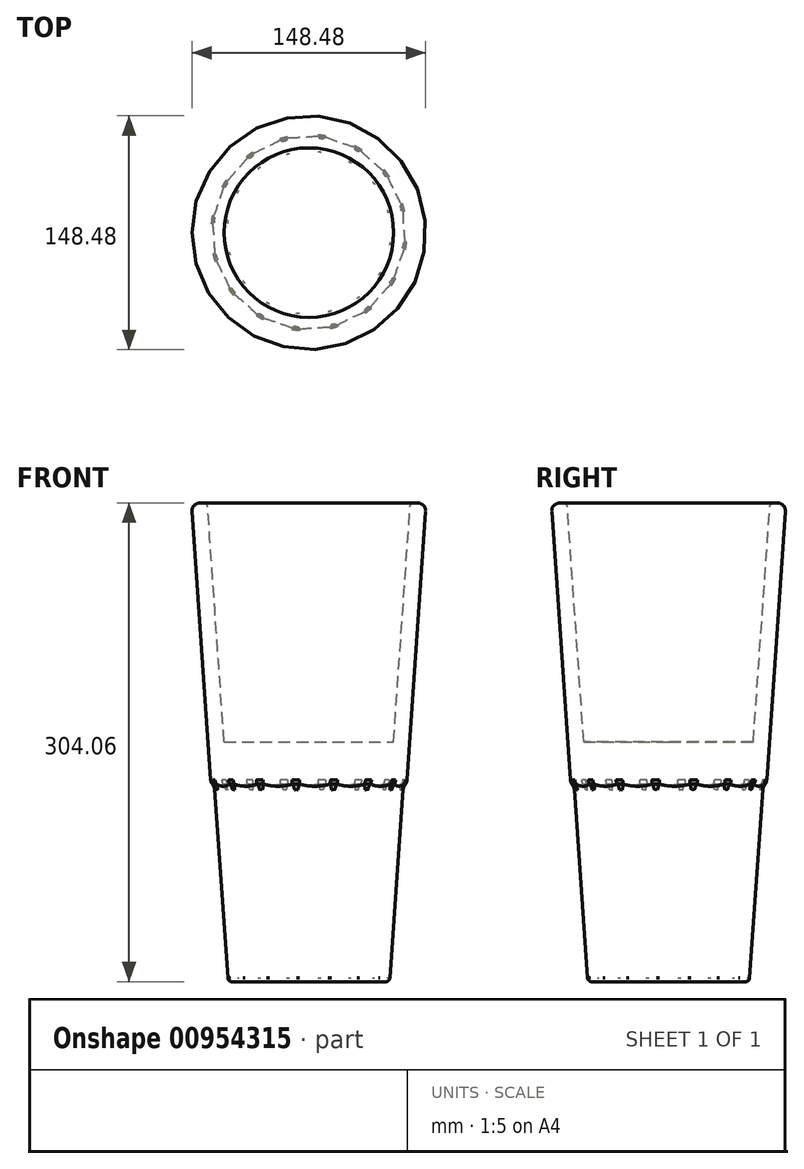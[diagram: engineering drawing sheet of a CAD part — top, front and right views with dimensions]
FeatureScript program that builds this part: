
annotation { "Feature Type Name" : "Feature", "Feature Type Description" : "" }
export const myFeature = defineFeature(function(context is Context, id is Id, definition is map)
    precondition{}
    {
        {
            var Q0;
            Q0=qCreatedBy(makeId("Front.planeOp"),FACE);
            var sketch = newSketch(context, id + "F0", { "sketchPlane" : qUnion([Q0])});
            skLineSegment(sketch, "E0", {"start": v(0, 0) * mm, "end": v(21.26, 304.06) * mm});
            skLineSegment(sketch, "E1", {"start": v(21.26, 304.06) * mm, "end": v(31.42, 304.06) * mm});
            skLineSegment(sketch, "E2", {"start": v(31.42, 304.06) * mm, "end": v(19.02, 126.7) * mm});
            skLineSegment(sketch, "E3", {"start": v(19.02, 126.7) * mm, "end": v(16.18, 122.48) * mm});
            skLineSegment(sketch, "E4", {"start": v(16.18, 122.48) * mm, "end": v(7.61, 0) * mm});
            skLineSegment(sketch, "E5", {"start": v(7.61, 0) * mm, "end": v(0, 0) * mm});
            skLineSegment(sketch, "E6.bottom", {"start": v(7.61, 0) * mm, "end": v(-43.19, 0) * mm});
            skLineSegment(sketch, "E6.top", {"start": v(7.61, 5.08) * mm, "end": v(-43.19, 5.08) * mm});
            skLineSegment(sketch, "E6.left", {"start": v(7.61, 0) * mm, "end": v(7.61, 5.08) * mm});
            skLineSegment(sketch, "E6.right", {"start": v(-43.19, 0) * mm, "end": v(-43.19, 5.08) * mm});
            skSolve(sketch);
        }
        {
            var Q0;
            {var subQ0=sQuery(id+"F0.wireOp",EDGE,"E1");Q0=makeQuery(id+"F0.imprint","IMPRINT",FACE,{"disambiguationData":[TD([[makeQuery(id+"F0.imprint","IMPRINT",EDGE,{"derivedFrom":subQ0}),-1.0]])]});}
            var Q1;
            {var subQ5=sQuery(id+"F0.wireOp",EDGE,"E6.left");Q1=makeQuery(id+"F0.imprint","IMPRINT",FACE,{"disambiguationData":[TD([[makeQuery(id+"F0.imprint","IMPRINT",EDGE,{"derivedFrom":subQ5}),1.0]])]});}
            var Q2;
            {var subQ5=sQuery(id+"F0.wireOp",EDGE,"E6.right");Q2=makeQuery(id+"F0.imprint","IMPRINT",FACE,{"disambiguationData":[TD([[makeQuery(id+"F0.imprint","IMPRINT",EDGE,{"derivedFrom":subQ5}),-1.0]])]});}
            var Q3;
            Q3=sQuery(id+"F0.wireOp",EDGE,"E6.right");
            revolve(context, id + "F1", {"surfaceOperationType" : NewSurfaceOperationType.NEW, "entities" : qUnion([Q0, Q1, Q2]), "axis" : qUnion([Q3]), "revolveType" : RevolveType.FULL});
        }
        {
            var Q0;
            Q0=makeQuery(id+"F1.opRevolve","SWEPT_FACE",FACE,{"disambiguationData":[OSD([sQuery(id+"F0.wireOp",EDGE,"E6.bottom")])]});
            var sketch = newSketch(context, id + "F2", { "sketchPlane" : qUnion([Q0])});
            skCircle(sketch, "E7.cCircle", {"center": v(-43.19, 0) * mm, "radius": 50.8 * mm, "construction": true});
            skLineSegment(sketch, "E7.0", {"start": v(1.6, 26) * mm, "end": v(8.15, 6.88) * mm});
            skLineSegment(sketch, "E7.1", {"start": v(8.15, 6.88) * mm, "end": v(6.88, -13.29) * mm});
            skLineSegment(sketch, "E7.2", {"start": v(6.88, -13.29) * mm, "end": v(-2.02, -31.43) * mm});
            skLineSegment(sketch, "E7.3", {"start": v(-2.02, -31.43) * mm, "end": v(-17.18, -44.8) * mm});
            skLineSegment(sketch, "E7.4", {"start": v(-17.18, -44.8) * mm, "end": v(-36.3, -51.34) * mm});
            skLineSegment(sketch, "E7.5", {"start": v(-36.3, -51.34) * mm, "end": v(-56.47, -50.06) * mm});
            skLineSegment(sketch, "E7.6", {"start": v(-56.47, -50.06) * mm, "end": v(-74.62, -41.17) * mm});
            skLineSegment(sketch, "E7.7", {"start": v(-74.62, -41.17) * mm, "end": v(-87.98, -26) * mm});
            skLineSegment(sketch, "E7.8", {"start": v(-87.98, -26) * mm, "end": v(-94.52, -6.88) * mm});
            skLineSegment(sketch, "E7.9", {"start": v(-94.52, -6.88) * mm, "end": v(-93.25, 13.29) * mm});
            skLineSegment(sketch, "E7.10", {"start": v(-93.25, 13.29) * mm, "end": v(-84.35, 31.43) * mm});
            skLineSegment(sketch, "E7.11", {"start": v(-84.35, 31.43) * mm, "end": v(-69.2, 44.8) * mm});
            skLineSegment(sketch, "E7.12", {"start": v(-69.2, 44.8) * mm, "end": v(-50.07, 51.34) * mm});
            skLineSegment(sketch, "E7.13", {"start": v(-50.07, 51.34) * mm, "end": v(-29.9, 50.06) * mm});
            skLineSegment(sketch, "E7.14", {"start": v(-29.9, 50.06) * mm, "end": v(-11.75, 41.17) * mm});
            skLineSegment(sketch, "E7.15", {"start": v(-11.75, 41.17) * mm, "end": v(1.6, 26) * mm});
            skPoint(sketch, "E7.0.midPoint", {"position": v(4.88, 16.44) * mm});
            skCircle(sketch, "E8", {"center": v(-43.19, 0) * mm, "radius": 50.8 * mm});
            skSolve(sketch);
        }
        {
            var Q0;
            Q0 = qSketchRegion(id + "F2", true);
            extrude(context, id + "F3", {"entities" : qUnion([Q0]), "operationType" : NewBodyOperationType.ADD, "oppositeDirection" : true, "depth" : 152.4 * mm, "offsetDistance" : 25.4 * mm, "hasDraft" : true, "draftAngle" : 4 * degree});
        }
        {
            var Q0;
            Q0=makeQuery(id+"F3.opExtrude","SWEPT_EDGE",EDGE,{"disambiguationData":[OSD([sQuery(id+"F2.wireOp",EDGE,"E7.1"),sQuery(id+"F2.wireOp",EDGE,"E7.2")])]});
            fillet(context, id + "F4", {"entities" : qUnion([Q0]), "radius" : 5.08 * mm, "tangentPropagation" : true, "allowEdgeOverflow" : false});
        }
        {
            var Q0;
            Q0=makeQuery(id+"F3.opExtrude","SWEPT_EDGE",EDGE,{"disambiguationData":[OSD([sQuery(id+"F2.wireOp",EDGE,"E7.2"),sQuery(id+"F2.wireOp",EDGE,"E7.3")])]});
            var Q1;
            Q1=makeQuery(id+"F3.opExtrude","SWEPT_EDGE",EDGE,{"disambiguationData":[OSD([sQuery(id+"F2.wireOp",EDGE,"E7.3"),sQuery(id+"F2.wireOp",EDGE,"E7.4")])]});
            var Q2;
            Q2=makeQuery(id+"F3.opExtrude","SWEPT_EDGE",EDGE,{"disambiguationData":[OSD([sQuery(id+"F2.wireOp",EDGE,"E7.4"),sQuery(id+"F2.wireOp",EDGE,"E7.5")])]});
            var Q3;
            Q3=makeQuery(id+"F3.opExtrude","SWEPT_EDGE",EDGE,{"disambiguationData":[OSD([sQuery(id+"F2.wireOp",EDGE,"E7.0"),sQuery(id+"F2.wireOp",EDGE,"E7.1")])]});
            var Q4;
            Q4=makeQuery(id+"F3.opExtrude","SWEPT_EDGE",EDGE,{"disambiguationData":[OSD([sQuery(id+"F2.wireOp",EDGE,"E7.0"),sQuery(id+"F2.wireOp",EDGE,"E7.15")])]});
            var Q5;
            Q5=makeQuery(id+"F3.opExtrude","SWEPT_EDGE",EDGE,{"disambiguationData":[OSD([sQuery(id+"F2.wireOp",EDGE,"E7.14"),sQuery(id+"F2.wireOp",EDGE,"E7.15")])]});
            var Q6;
            Q6=makeQuery(id+"F3.opExtrude","SWEPT_EDGE",EDGE,{"disambiguationData":[OSD([sQuery(id+"F2.wireOp",EDGE,"E7.13"),sQuery(id+"F2.wireOp",EDGE,"E7.14")])]});
            var Q7;
            Q7=makeQuery(id+"F3.opExtrude","SWEPT_EDGE",EDGE,{"disambiguationData":[OSD([sQuery(id+"F2.wireOp",EDGE,"E7.12"),sQuery(id+"F2.wireOp",EDGE,"E7.13")])]});
            var Q8;
            Q8=makeQuery(id+"F3.opExtrude","SWEPT_EDGE",EDGE,{"disambiguationData":[OSD([sQuery(id+"F2.wireOp",EDGE,"E7.11"),sQuery(id+"F2.wireOp",EDGE,"E7.12")])]});
            var Q9;
            Q9=makeQuery(id+"F3.opExtrude","SWEPT_EDGE",EDGE,{"disambiguationData":[OSD([sQuery(id+"F2.wireOp",EDGE,"E7.10"),sQuery(id+"F2.wireOp",EDGE,"E7.11")])]});
            var Q10;
            Q10=makeQuery(id+"F3.opExtrude","SWEPT_EDGE",EDGE,{"disambiguationData":[OSD([sQuery(id+"F2.wireOp",EDGE,"E7.9"),sQuery(id+"F2.wireOp",EDGE,"E7.10")])]});
            var Q11;
            Q11=makeQuery(id+"F3.opExtrude","SWEPT_EDGE",EDGE,{"disambiguationData":[OSD([sQuery(id+"F2.wireOp",EDGE,"E7.8"),sQuery(id+"F2.wireOp",EDGE,"E7.9")])]});
            var Q12;
            Q12=makeQuery(id+"F3.opExtrude","SWEPT_EDGE",EDGE,{"disambiguationData":[OSD([sQuery(id+"F2.wireOp",EDGE,"E7.7"),sQuery(id+"F2.wireOp",EDGE,"E7.8")])]});
            var Q13;
            Q13=makeQuery(id+"F3.opExtrude","SWEPT_EDGE",EDGE,{"disambiguationData":[OSD([sQuery(id+"F2.wireOp",EDGE,"E7.6"),sQuery(id+"F2.wireOp",EDGE,"E7.7")])]});
            var Q14;
            Q14=makeQuery(id+"F3.opExtrude","SWEPT_EDGE",EDGE,{"disambiguationData":[OSD([sQuery(id+"F2.wireOp",EDGE,"E7.5"),sQuery(id+"F2.wireOp",EDGE,"E7.6")])]});
            fillet(context, id + "F5", {"entities" : qUnion([Q0, Q1, Q2, Q3, Q4, Q5, Q6, Q7, Q8, Q9, Q10, Q11, Q12, Q13, Q14]), "radius" : 5.08 * mm, "tangentPropagation" : true, "allowEdgeOverflow" : false});
        }
        {
            var Q0;
            Q0=makeQuery(id+"F3.opExtrude","CAP_EDGE",EDGE,{"disambiguationData":[OSD([sQuery(id+"F2.wireOp",EDGE,"E7.5")])],"isStart":true});
            fillet(context, id + "F6", {"entities" : qUnion([Q0]), "radius" : 2.54 * mm, "tangentPropagation" : true, "allowEdgeOverflow" : false});
        }
        {
            var Q0;
            Q0=makeQuery(id+"F3.boolean.opBoolean","INTERSECT",EDGE,{"derivedFrom":[makeQuery(id+"F1.opRevolve","SWEPT_FACE",FACE,{"disambiguationData":[OSD([sQuery(id+"F0.wireOp",EDGE,"E3")])]}),makeQuery(id+"F3.opExtrude","SWEPT_FACE",FACE,{"disambiguationData":[OSD([sQuery(id+"F2.wireOp",EDGE,"E7.6")])]})]});
            fillet(context, id + "F7", {"entities" : qUnion([Q0]), "radius" : 7.62 * mm, "tangentPropagation" : true, "allowEdgeOverflow" : false});
        }
        {
            var Q0;
            Q0=makeQuery(id+"F1.opRevolve","SWEPT_EDGE",EDGE,{"disambiguationData":[OSD([sQuery(id+"F0.wireOp",EDGE,"E2"),sQuery(id+"F0.wireOp",EDGE,"E3")])]});
            fillet(context, id + "F8", {"entities" : qUnion([Q0]), "radius" : 5.08 * mm, "tangentPropagation" : true, "allowEdgeOverflow" : false});
        }
        {
            var Q0;
            Q0=makeQuery(id+"F1.opRevolve","SWEPT_EDGE",EDGE,{"disambiguationData":[OSD([sQuery(id+"F0.wireOp",EDGE,"E1"),sQuery(id+"F0.wireOp",EDGE,"E2")])]});
            fillet(context, id + "F9", {"entities" : qUnion([Q0]), "radius" : 5.08 * mm, "tangentPropagation" : true, "allowEdgeOverflow" : false});
        }
        {
            var Q0;
            Q0=makeQuery(id+"F1.opRevolve","SWEPT_EDGE",EDGE,{"disambiguationData":[OSD([sQuery(id+"F0.wireOp",EDGE,"E0"),sQuery(id+"F0.wireOp",EDGE,"E1")])]});
            fillet(context, id + "F10", {"entities" : qUnion([Q0]), "radius" : 2.54 * mm, "tangentPropagation" : true, "allowEdgeOverflow" : false});
        }
    });
